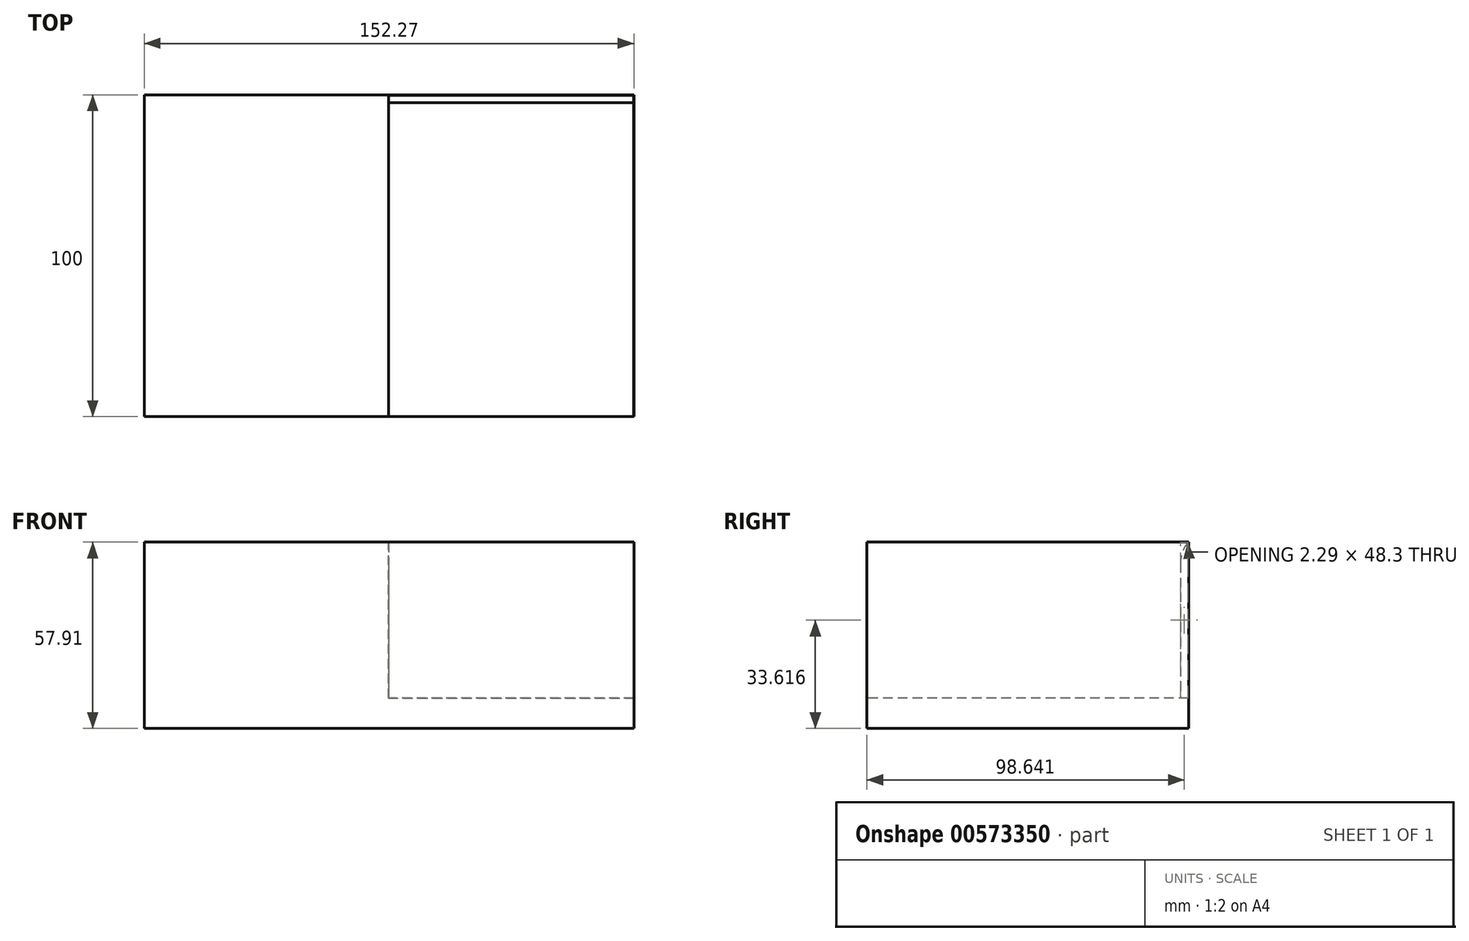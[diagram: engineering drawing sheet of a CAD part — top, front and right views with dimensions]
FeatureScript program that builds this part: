
annotation { "Feature Type Name" : "Feature", "Feature Type Description" : "" }
export const myFeature = defineFeature(function(context is Context, id is Id, definition is map)
    precondition{}
    {
        {
            var Q0;
            Q0=qCreatedBy(makeId("Top.planeOp"),FACE);
            var sketch = newSketch(context, id + "F0", { "sketchPlane" : qUnion([Q0])});
            skLineSegment(sketch, "E0", {"start": v(0, -50) * mm, "end": v(76.32, -50) * mm});
            skLineSegment(sketch, "E1", {"start": v(76.32, -50) * mm, "end": v(76.32, 50) * mm});
            skLineSegment(sketch, "E2", {"start": v(76.32, 50) * mm, "end": v(0, 50) * mm});
            skLineSegment(sketch, "E3", {"start": v(0, 50) * mm, "end": v(-75.95, 50) * mm});
            skLineSegment(sketch, "E4", {"start": v(-75.95, 50) * mm, "end": v(-75.95, -50) * mm});
            skLineSegment(sketch, "E5", {"start": v(-75.95, -50) * mm, "end": v(0, -50) * mm});
            skLineSegment(sketch, "E6", {"start": v(0, 50) * mm, "end": v(0, 0) * mm});
            skLineSegment(sketch, "E7", {"start": v(0, 0) * mm, "end": v(0, -50) * mm});
            skSolve(sketch);
        }
        {
            var Q0;
            Q0 = qSketchRegion(id + "F0", true);
            extrude(context, id + "F1", {"entities" : qUnion([Q0]), "depth" : 25.4 * mm, "offsetDistance" : 25.4 * mm, "hasSecondDirection" : true, "secondDirectionOppositeDirection" : true, "secondDirectionDepth" : 32.5 * mm});
        }
        {
            var Q0;
            Q0=qCreatedBy(makeId("Top.planeOp"),FACE);
            var sketch = newSketch(context, id + "F2", { "sketchPlane" : qUnion([Q0])});
            skLineSegment(sketch, "E8", {"start": v(0, 0) * mm, "end": v(0, -49.96) * mm});
            skLineSegment(sketch, "E9", {"start": v(0, -49.96) * mm, "end": v(76.2, -49.96) * mm});
            skLineSegment(sketch, "E10", {"start": v(76.2, -49.96) * mm, "end": v(76.2, 50.14) * mm});
            skLineSegment(sketch, "E11", {"start": v(76.2, 50.14) * mm, "end": v(0, 50.14) * mm});
            skLineSegment(sketch, "E12", {"start": v(0, 50.14) * mm, "end": v(0, 0) * mm});
            skSolve(sketch);
        }
        {
            var Q0;
            Q0 = qSketchRegion(id + "F2", true);
            extrude(context, id + "F3", {"entities" : qUnion([Q0]), "depth" : 39.37 * mm, "offsetDistance" : 25.4 * mm, "hasSecondDirection" : true, "secondDirectionOppositeDirection" : true, "secondDirectionDepth" : 23.1 * mm});
        }
        {
            var Q0;
            Q0=makeQuery(id+"F3.opExtrude","SWEPT_BODY",BODY,{"disambiguationData":[OSD([sQuery(id+"F2.wireOp",EDGE,"E8"),sQuery(id+"F2.wireOp",EDGE,"E9"),sQuery(id+"F2.wireOp",EDGE,"E10"),sQuery(id+"F2.wireOp",EDGE,"E11"),sQuery(id+"F2.wireOp",EDGE,"E12")])]});
            var Q1;
            Q1=makeQuery(id+"F1.opExtrude","SWEPT_BODY",BODY,{"disambiguationData":[OSD([sQuery(id+"F0.wireOp",EDGE,"E0"),sQuery(id+"F0.wireOp",EDGE,"E1"),sQuery(id+"F0.wireOp",EDGE,"E2"),sQuery(id+"F0.wireOp",EDGE,"E3"),sQuery(id+"F0.wireOp",EDGE,"E4"),sQuery(id+"F0.wireOp",EDGE,"E5")])]});
            booleanBodies(context, id + "F4", {"operationType" : BooleanOperationType.SUBTRACTION, "tools" : qUnion([Q0]), "targets" : qUnion([Q1])});
        }
        {
            var Q0;
            Q0=qCreatedBy(makeId("Front.planeOp"),FACE);
            var sketch = newSketch(context, id + "F5", { "sketchPlane" : qUnion([Q0])});
            skLineSegment(sketch, "E13", {"start": v(0, 25.26) * mm, "end": v(0, -23.04) * mm});
            skLineSegment(sketch, "E14", {"start": v(0, -23.04) * mm, "end": v(76.2, -23.04) * mm});
            skLineSegment(sketch, "E15", {"start": v(76.2, -23.04) * mm, "end": v(76.2, 25.26) * mm});
            skLineSegment(sketch, "E16", {"start": v(76.2, 25.26) * mm, "end": v(0, 25.26) * mm});
            skSolve(sketch);
        }
        {
            var Q0;
            Q0 = qSketchRegion(id + "F5", true);
            extrude(context, id + "F6", {"entities" : qUnion([Q0]), "operationType" : NewBodyOperationType.ADD, "oppositeDirection" : true, "depth" : 49.78 * mm, "offsetDistance" : 25.4 * mm, "hasSecondDirection" : true, "secondDirectionOppositeDirection" : true, "secondDirectionDepth" : 47.5 * mm});
        }
        {
            var Q0;
            Q0=makeQuery(id+"F6.opExtrude","CAP_EDGE",EDGE,{"disambiguationData":[OSD([sQuery(id+"F5.wireOp",EDGE,"E16")])],"isStart":true});
            fillet(context, id + "F7", {"entities" : qUnion([Q0]), "radius" : 10 * mm, "tangentPropagation" : true, "allowEdgeOverflow" : false});
        }
    });
